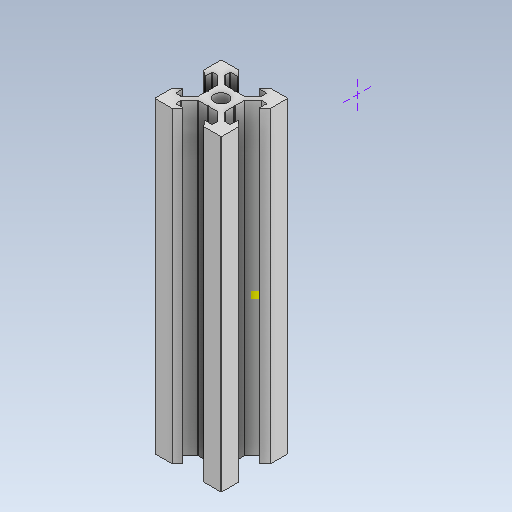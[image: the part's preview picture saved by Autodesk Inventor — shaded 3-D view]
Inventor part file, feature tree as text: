
AUTODESK INVENTOR PART (.ipt)
format: ipt  version: 2021 (Build 250183000, 183)  size: 237,568 bytes
history: native  units: mm
features: sketch x4, extrude x2, fillet x2, other x1, pattern_circular x1, hole x1, projected_geometry x1
ambient origin geometry x8: Origin, YZ Plane, XZ Plane, XY Plane, X Axis, Y Axis, Z Axis, Center Point
bodies: Body1 (feature_tree)
feature tree (12):
  other  "實體1"
  extrude  "擠出1"  Depth=20.0mm
  extrude  "擠出2"  Depth=20.0mm
  fillet  "圓角1"  Radius=92.5mm
  pattern_circular  "環形陣列1"  [2 undecoded]
  hole  "孔1"  [1 undecoded]
  fillet  "圓角2"  Radius=6.2mm
  sketch  "草圖4"
  sketch  "草圖1"
  sketch  "草圖2"
  projected_geometry  "投影迴路1"
  sketch  "草圖3"
note: 3 required parameter values undecoded (feature->parameter linkage not recoverable at this tier; creation-order binding heuristic only, values carry confidence <= 0.55)
